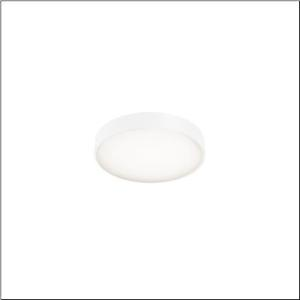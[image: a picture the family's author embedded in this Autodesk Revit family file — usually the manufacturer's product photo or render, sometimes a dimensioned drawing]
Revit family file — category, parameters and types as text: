
# Revit family: round_21_s_51mr34gd0421w
name_source: partatom
category: Lighting Fixtures
units: mm (PartAtom-declared; Revit-internal decimal feet)

## family parameters
Cut with Voids When Loaded = No
Host = Face
Light Source = No
Part Type = Normal
Room Calculation Point = No
Round Connector Dimension = Use Diameter
Shared = No

## types (1)
- Round 21 S (1 x LED, 4090 lm, 28.3 W, 4000K)
    Apparent Load = 28 VA
    CIE Flux Codes = 49 80 96 79 100
    Color Rendering = 80
    Color Temperature = 4000K
    Default Elevation = 1800 mm
    Description = Round 21 S, wall and ceiling luminaire, primary optical cover: cover, of PMMA, opal, light emission: direct/indirect distribution, primary light characteristic: symmetric, installation type: suspended mounting, surface-mounted, LED, rated luminous flux: 4.090lm, luminous efficacy: 135lm/W, light colour: 840, colour temperature: 4000K, control gear: DALI 2, with terminal, 5-pole, mains connection: 230V, AC, 50/60Hz, rated input power: 28.3W, housing, of aluminium, coated, white, diameter: 400mm, height: 62mm, protection rating (complete): IP40, insulation class (complete): insulation class I (protective earthing), certification: CE, impact resistance: IK04, permissible operating ambient temperature: -10..+35°C, packaging unit: 1 piece
    Height = 87 mm
    Lamp = 1 x LED
    Lamp Light Flux = 4090 lm
    Lamp Power = 28.3 W
    Lamp count = 1
    Length = 400 mm
    Luminous efficacy = 145 lm/W
    Manufacturer = Siteco
    ModVariant = No
    Model = 51MR34GD0421W
    Mounting Place = Wall
    Mounting Type = Surface mounted
    Number of Poles = 1
    OnlyDefault = Yes
    Power Factor = 1
    Product Name = Round 21 S
    Product group = wall and ceiling luminaire
    ProductGroupID = 2001
    Protection Class = Protection class I
    Protection Degree = IP 40
    RLX_Detail_Level = 1
    RLX_Emergency_Light_Flux = 0 lm
    RLX_Emergency_Type = 0
    RLX_Emergency_Type_DB = No
    RlxData = <blob elided: 9929 chars, md5=ef229e9d>
    Socket = socket
    Standby Power = 0 W
    System Light Flux = 4090 lm
    System Power = 28 W
    Type Comments = Product without accessories
    Type Image = l_1258307.jpg
    URL = http://relux.com
    VarID = ---
    Voltage = 0 V
    Weight = 0.00 kg
    Width = 0 mm  [stored 0 ft]

note: [stored X ft] marks values corroborated as IEEE doubles in the binary element streams (Revit-internal decimal feet)

## geometry (parser evidence)
native form markers: Sweep x11
no freeform markers — native parametric forms only
